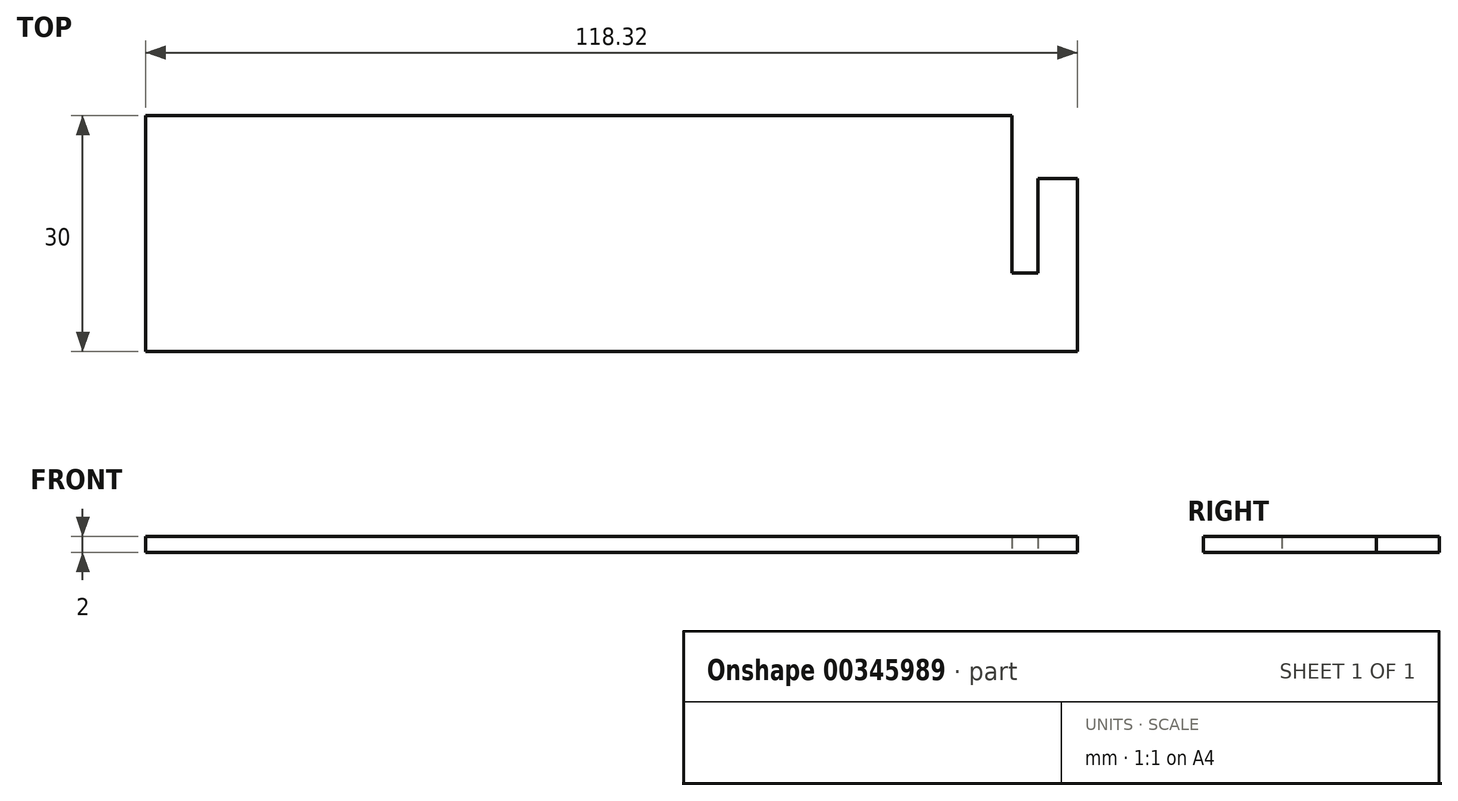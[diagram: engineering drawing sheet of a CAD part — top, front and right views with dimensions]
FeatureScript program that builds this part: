
annotation { "Feature Type Name" : "Feature", "Feature Type Description" : "" }
export const myFeature = defineFeature(function(context is Context, id is Id, definition is map)
    precondition{}
    {
        {
            var Q0;
            Q0=qCreatedBy(makeId("Top.planeOp"),FACE);
            var sketch = newSketch(context, id + "F0", { "sketchPlane" : qUnion([Q0])});
            skLineSegment(sketch, "E0.bottom", {"start": v(-55, 15) * mm, "end": v(55, 15) * mm});
            skLineSegment(sketch, "E0.top", {"start": v(-55, -15) * mm, "end": v(55, -15) * mm});
            skLineSegment(sketch, "E0.left", {"start": v(-55, 15) * mm, "end": v(-55, -15) * mm});
            skLineSegment(sketch, "E0.right", {"start": v(55, 15) * mm, "end": v(55, -15) * mm});
            skPoint(sketch, "E0.middle", {"position": v(0, 0) * mm});
            skLineSegment(sketch, "E1", {"start": v(55, -5) * mm, "end": v(63.32, -5) * mm});
            skLineSegment(sketch, "E2", {"start": v(63.32, -5) * mm, "end": v(63.32, -15) * mm});
            skLineSegment(sketch, "E3", {"start": v(63.32, -15) * mm, "end": v(55, -15) * mm});
            skLineSegment(sketch, "E4", {"start": v(63.32, -5) * mm, "end": v(63.32, 7) * mm});
            skLineSegment(sketch, "E5", {"start": v(63.32, 7) * mm, "end": v(58.32, 7) * mm});
            skLineSegment(sketch, "E6", {"start": v(58.32, 7) * mm, "end": v(58.32, -5) * mm});
            skSolve(sketch);
        }
        {
            var Q0;
            Q0 = qSketchRegion(id + "F0", true);
            extrude(context, id + "F1", {"entities" : qUnion([Q0]), "depth" : 2 * mm});
        }
    });
